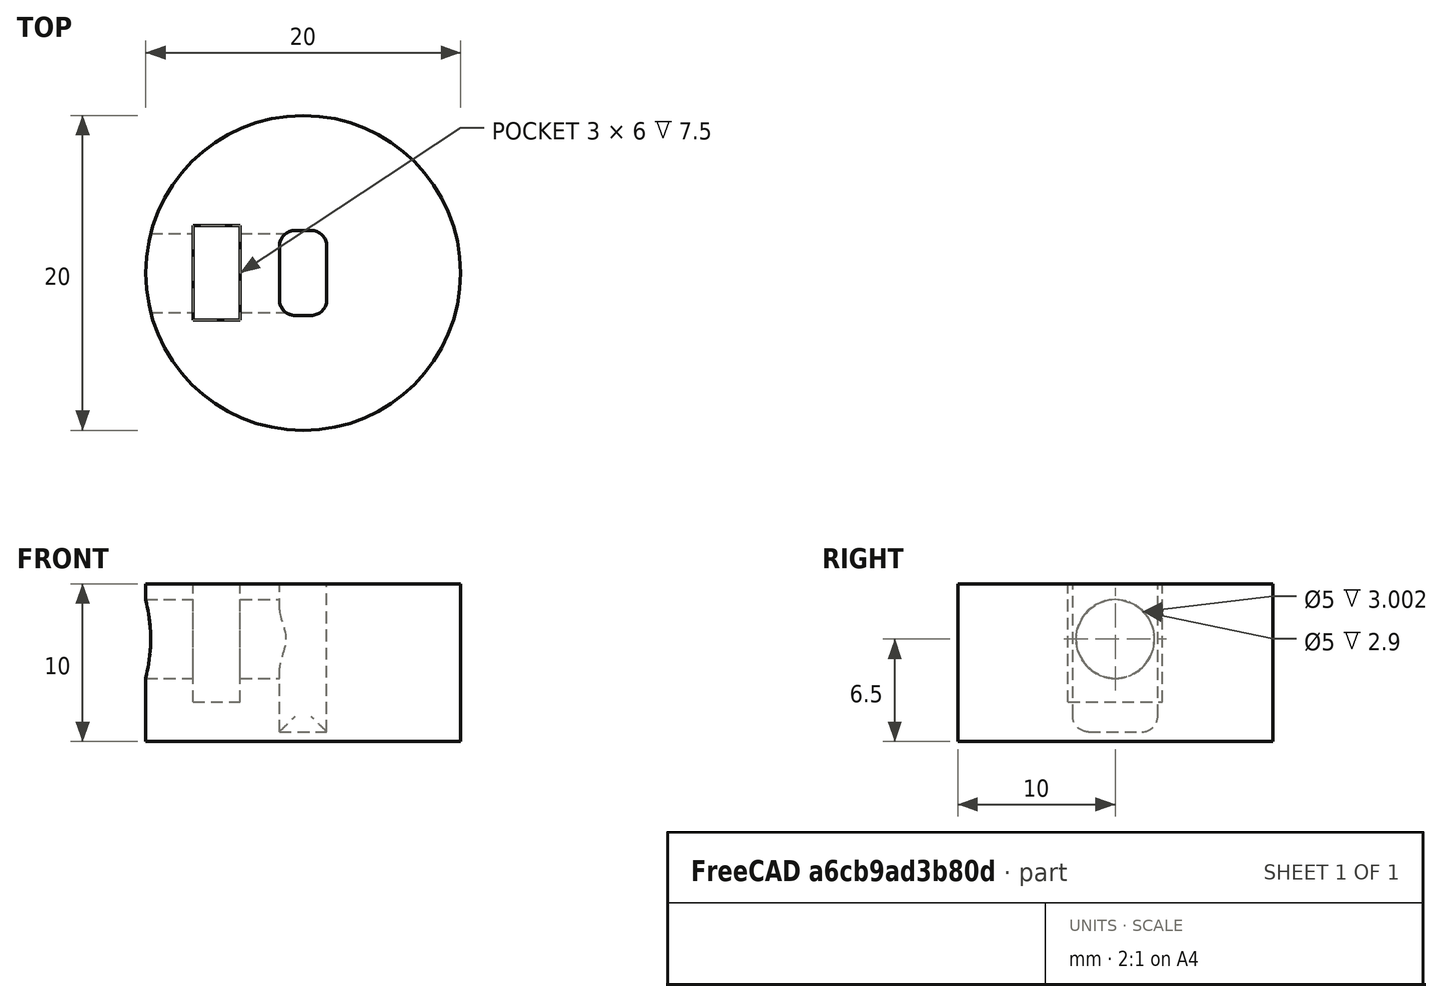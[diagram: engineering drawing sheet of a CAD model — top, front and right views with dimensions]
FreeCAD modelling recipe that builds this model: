
FCSTD DOCUMENT  (FreeCAD 0.18.4R)
Label: soporte_motor
License: All rights reserved
LicenseURL: http://en.wikipedia.org/wiki/All_rights_reserved
objects: Part::Cut×3, Part::Cylinder×2, Part::Box×2, Part::Fillet×1
note: 8 computed .brp shape members not serialized (recipe doc carries the construction recipe); baked Part::Feature solids carry a one-line shape summary decoded from their .brp

FEATURE [Part::Cylinder] Cylinder  label="Cilindro"
  Angle = 360
  AttacherType = Attacher::AttachEngine3D
  Height = 10
  Radius = 10
FEATURE [Part::Box] Box  label="Cubo"
  AttacherType = Attacher::AttachEngine3D
  Height = 15
  Length = 3
  Placement = pos=(-1.5,-2.7,0.6) rot=(0,0,1;0rad)
  Width = 5.4
FEATURE [Part::Box] Box001  label="Cubo001"
  AttacherType = Attacher::AttachEngine3D
  Height = 15
  Length = 3
  Placement = pos=(-7,-3,2.5) rot=(0,0,1;0rad)
  Width = 6
FEATURE [Part::Cylinder] Cylinder001  label="Cilindro001"
  Angle = 360
  AttacherType = Attacher::AttachEngine3D
  Height = 15
  Placement = pos=(-15,0,6.5) rot=(0,1,0;1.5708rad)
  Radius = 2.5
FEATURE [Part::Fillet] Fillet
  Base = -> Box
  Edges = 8 edges r=1: [Edge1,Edge3,Edge5,Edge7,Edge9,Edge10,Edge11,Edge12]
FEATURE [Part::Cut] Cut
  Base = -> Cylinder
  Tool = -> Box001
FEATURE [Part::Cut] Cut001
  Base = -> Cut
  Tool = -> Fillet
FEATURE [Part::Cut] Cut002
  Base = -> Cut001
  Tool = -> Cylinder001
